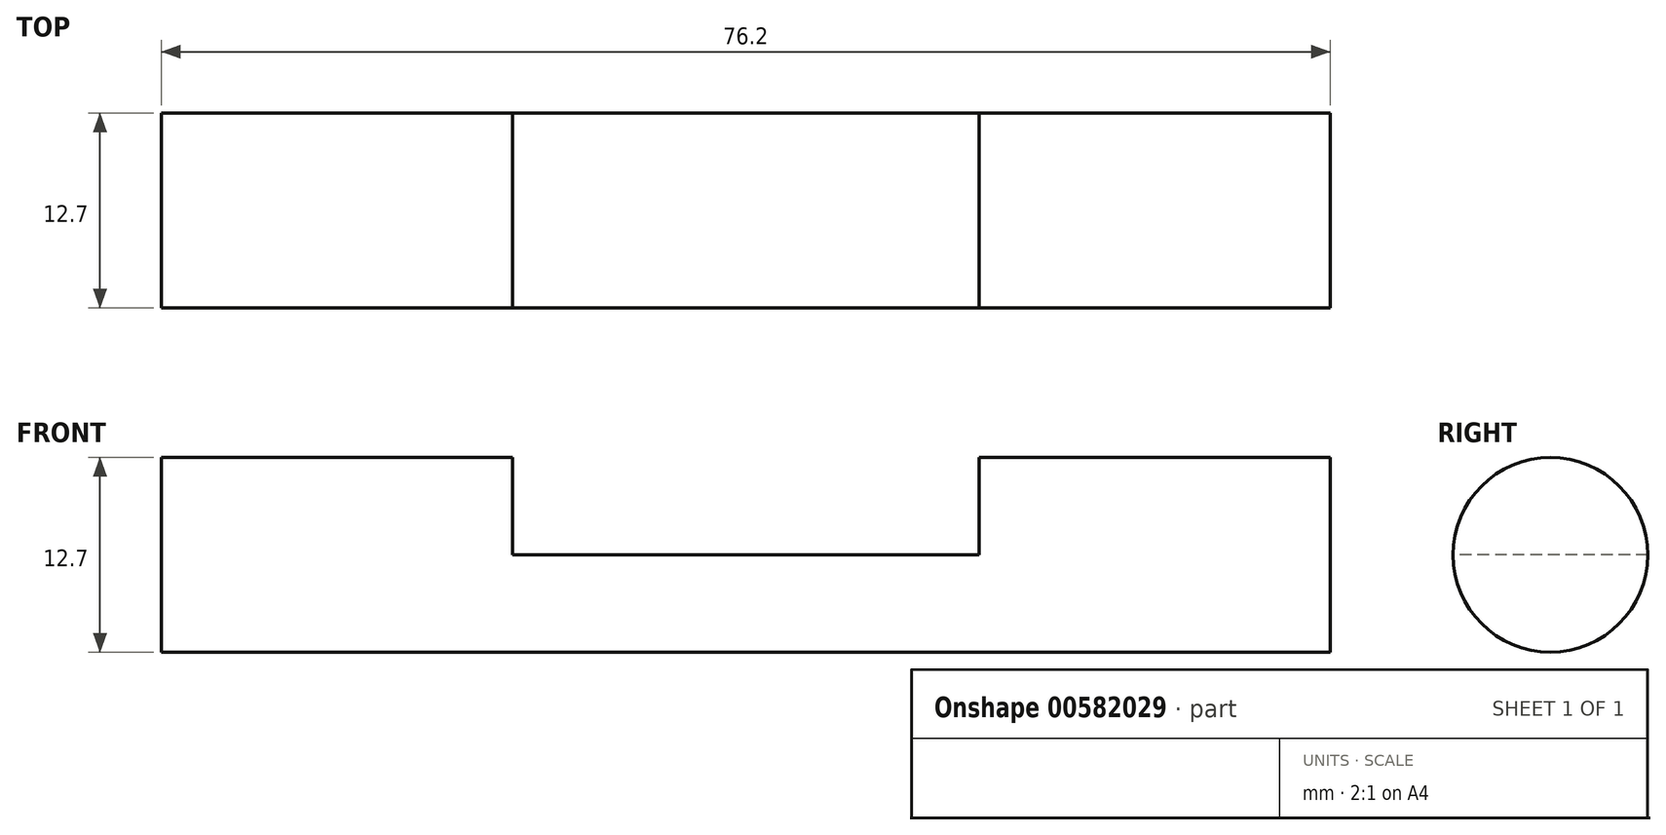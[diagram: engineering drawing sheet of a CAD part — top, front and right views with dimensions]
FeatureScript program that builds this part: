
annotation { "Feature Type Name" : "Feature", "Feature Type Description" : "" }
export const myFeature = defineFeature(function(context is Context, id is Id, definition is map)
    precondition{}
    {
        {
            var Q0;
            Q0=qCreatedBy(makeId("Right.planeOp"),FACE);
            var sketch = newSketch(context, id + "F0", { "sketchPlane" : qUnion([Q0])});
            skCircle(sketch, "E0", {"center": v(0, 0) * mm, "radius": 6.35 * mm});
            skSolve(sketch);
        }
        {
            var Q0;
            Q0 = qSketchRegion(id + "F0", true);
            extrude(context, id + "F1", {"entities" : qUnion([Q0]), "depth" : 76.2 * mm, "offsetDistance" : 25.4 * mm, "symmetric" : true});
        }
        {
            var Q0;
            Q0=qCreatedBy(makeId("Front.planeOp"),FACE);
            var sketch = newSketch(context, id + "F2", { "sketchPlane" : qUnion([Q0])});
            skLineSegment(sketch, "E1.bottom", {"start": v(-15.2, 7.06) * mm, "end": v(15.2, 7.06) * mm});
            skLineSegment(sketch, "E1.top", {"start": v(-15.2, 0) * mm, "end": v(15.2, 0) * mm});
            skLineSegment(sketch, "E1.left", {"start": v(-15.2, 7.06) * mm, "end": v(-15.2, 0) * mm});
            skLineSegment(sketch, "E1.right", {"start": v(15.2, 7.06) * mm, "end": v(15.2, 0) * mm});
            skSolve(sketch);
        }
        {
            var Q0;
            Q0 = qSketchRegion(id + "F2", true);
            extrude(context, id + "F3", {"entities" : qUnion([Q0]), "operationType" : NewBodyOperationType.REMOVE, "oppositeDirection" : true, "depth" : 50.8 * mm, "offsetDistance" : 25.4 * mm, "symmetric" : true});
        }
    });
